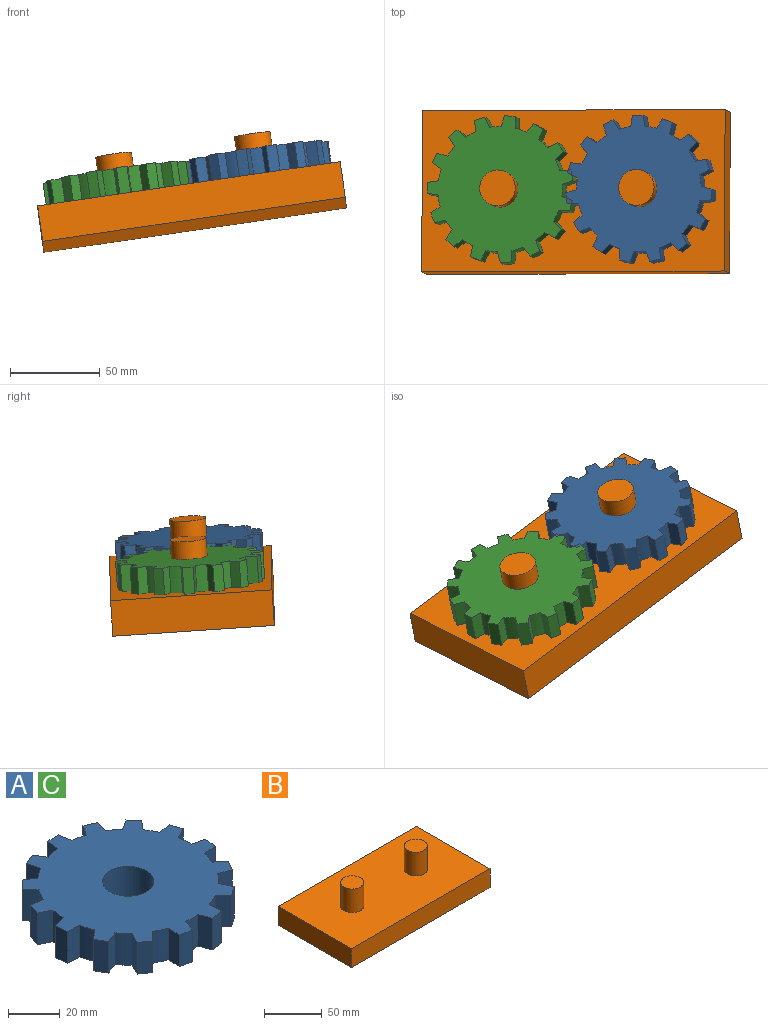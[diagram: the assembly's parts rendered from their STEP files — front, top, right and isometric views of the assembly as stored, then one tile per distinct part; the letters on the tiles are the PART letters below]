
ASSEMBLY  parts=3 mates=2
PART A: 63 faces, bbox 82.2x81.7x15 mm
  f0: plane 15x5.48mm, normal (-0.41,0.91,0), area 90mm2, adj f1,f2,f3,f4
  f1: plane 15x6.1mm, normal (-0.97,-0.26,0), area 94.6mm2, adj f0,f3,f4,f5
  f2: plane 15x5.29mm, normal (0.84,0.55,0), area 94.6mm2, adj f0,f3,f4,f61
  f3: plane 82.18x81.73mm, normal (0,0,1), area 4169.7mm2, adj f0,f1,f2,f5,f6,f7,f8,f9
  f4: plane 82.18x81.73mm, normal (0,0,-1), area 4169.7mm2, adj f0,f1,f2,f5,f6,f7,f8,f9
  f5: cylinder r=35mm len=15mm, axis (0,0,-1), area 99.7mm2, adj f1,f3,f4,f8
  f6: plane 15x4.46mm, normal (-0.74,0.67,0), area 90mm2, adj f3,f4,f7,f8
  f7: plane 15x4.91mm, normal (-0.78,-0.63,0), area 94.6mm2, adj f3,f4,f6,f9
  f8: plane 15x5.29mm, normal (0.54,0.84,0), area 94.6mm2, adj f3,f4,f5,f6
  f9: cylinder r=35mm len=15mm, axis (0,0,-1), area 99.7mm2, adj f3,f4,f7,f12
  f10: plane 15x5.71mm, normal (-0.95,0.31,0), area 90mm2, adj f3,f4,f11,f12
  f11: plane 15x5.62mm, normal (-0.46,-0.89,0), area 94.6mm2, adj f3,f4,f10,f13
  f12: plane 15x6.23mm, normal (0.16,0.99,0), area 94.6mm2, adj f3,f4,f9,f10
  f13: cylinder r=35mm len=15mm, axis (0,0,-1), area 99.7mm2, adj f3,f4,f11,f16
  f14: plane 15x5.97mm, normal (-0.99,-0.1,0), area 90mm2, adj f3,f4,f15,f16
  f15: plane 15x6.3mm, normal (-0.05,-1,0), area 94.6mm2, adj f3,f4,f14,f17
  f16: plane 15x6.09mm, normal (-0.26,0.97,0), area 94.6mm2, adj f3,f4,f13,f14
  f17: cylinder r=35mm len=15mm, axis (0,0,-1), area 99.7mm2, adj f3,f4,f15,f20
  f18: plane 15x5.2mm, normal (-0.87,-0.5,0), area 90mm2, adj f3,f4,f19,f20
  f19: plane 15x5.89mm, normal (0.36,-0.93,0), area 94.6mm2, adj f3,f4,f18,f21
  f20: plane 15x4.9mm, normal (-0.63,0.78,0), area 94.6mm2, adj f3,f4,f17,f18
  f21: cylinder r=35mm len=15mm, axis (0,0,-1), area 99.7mm2, adj f3,f4,f19,f24
  f22: plane 15x4.85mm, normal (-0.59,-0.81,0), area 90mm2, adj f3,f4,f23,f24
  f23: plane 15x4.47mm, normal (0.71,-0.71,0), area 94.6mm2, adj f3,f4,f22,f25
  f24: plane 15x5.62mm, normal (-0.89,0.45,0), area 94.6mm2, adj f3,f4,f21,f22
  f25: cylinder r=35mm len=15mm, axis (0,0,-1), area 99.7mm2, adj f3,f4,f23,f28
  f26: plane 15x5.87mm, normal (-0.21,-0.98,0), area 90mm2, adj f3,f4,f27,f28
  f27: plane 15x5.89mm, normal (0.93,-0.36,0), area 94.6mm2, adj f3,f4,f26,f29
  f28: plane 15x6.3mm, normal (-1,0.05,0), area 94.6mm2, adj f3,f4,f25,f26
  f29: cylinder r=35mm len=15mm, axis (0,0,-1), area 99.7mm2, adj f3,f4,f27,f32
  f30: plane 15x5.87mm, normal (0.21,-0.98,0), area 90mm2, adj f3,f4,f31,f32
  f31: plane 15x6.3mm, normal (1,0.05,0), area 94.6mm2, adj f3,f4,f30,f33
  f32: plane 15x5.89mm, normal (-0.93,-0.36,0), area 94.6mm2, adj f3,f4,f29,f30
  f33: cylinder r=35mm len=15mm, axis (0,0,-1), area 99.7mm2, adj f3,f4,f31,f36
  f34: plane 15x4.85mm, normal (0.59,-0.81,0), area 90mm2, adj f3,f4,f35,f36
  f35: plane 15x5.63mm, normal (0.89,0.45,0), area 94.6mm2, adj f3,f4,f34,f37
  f36: plane 15x4.46mm, normal (-0.71,-0.71,0), area 94.6mm2, adj f3,f4,f33,f34
  f37: cylinder r=35mm len=15mm, axis (0,0,-1), area 99.7mm2, adj f3,f4,f35,f40
  f38: plane 15x5.2mm, normal (0.87,-0.5,0), area 90mm2, adj f3,f4,f39,f40
  f39: plane 15x4.89mm, normal (0.63,0.78,0), area 94.6mm2, adj f3,f4,f38,f41
  f40: plane 15x5.89mm, normal (-0.36,-0.93,0), area 94.6mm2, adj f3,f4,f37,f38
  f41: cylinder r=35mm len=15mm, axis (0,0,-1), area 99.7mm2, adj f3,f4,f39,f44
  f42: plane 15x5.97mm, normal (0.99,-0.1,0), area 90mm2, adj f3,f4,f43,f44
  f43: plane 15x6.09mm, normal (0.26,0.97,0), area 94.6mm2, adj f3,f4,f42,f45
  f44: plane 15x6.3mm, normal (0.05,-1,0), area 94.6mm2, adj f3,f4,f41,f42
  f45: cylinder r=35mm len=15mm, axis (0,0,-1), area 99.7mm2, adj f3,f4,f43,f48
  f46: plane 15x5.71mm, normal (0.95,0.31,0), area 90mm2, adj f3,f4,f47,f48
  f47: plane 15x6.23mm, normal (-0.15,0.99,0), area 94.6mm2, adj f3,f4,f46,f49
  f48: plane 15x5.62mm, normal (0.45,-0.89,0), area 94.6mm2, adj f3,f4,f45,f46
  f49: cylinder r=35mm len=15mm, axis (0,0,-1), area 99.7mm2, adj f3,f4,f47,f52
  f50: plane 15x4.46mm, normal (0.74,0.67,0), area 90mm2, adj f3,f4,f51,f52
  f51: plane 15x5.3mm, normal (-0.54,0.84,0), area 94.6mm2, adj f3,f4,f50,f53
  f52: plane 15x4.91mm, normal (0.78,-0.63,0), area 94.6mm2, adj f3,f4,f49,f50
  f53: cylinder r=35mm len=15mm, axis (0,0,-1), area 99.7mm2, adj f3,f4,f51,f56
  f54: plane 15x5.48mm, normal (0.41,0.91,0), area 90mm2, adj f3,f4,f55,f56
  f55: plane 15x5.28mm, normal (-0.84,0.55,0), area 94.6mm2, adj f3,f4,f54,f57
  f56: plane 15x6.09mm, normal (0.97,-0.26,0), area 94.6mm2, adj f3,f4,f53,f54
  f57: cylinder r=35mm len=15mm, axis (0,0,-1), area 99.7mm2, adj f3,f4,f55,f60
  f58: plane 15x6mm, normal (0,1,0), area 90mm2, adj f3,f4,f59,f60
  f59: plane 15x6.23mm, normal (-0.99,0.16,0), area 94.6mm2, adj f3,f4,f58,f61
  f60: plane 15x6.23mm, normal (0.99,0.16,0), area 94.6mm2, adj f3,f4,f57,f58
  f61: cylinder r=35mm len=15mm, axis (0,0,-1), area 99.7mm2, adj f2,f3,f4,f59
  f62: cylinder r=10mm len=20mm, axis (0,0,1), area 942.5mm2, adj f3,f4
PART B: 10 faces, bbox 170x90x45 mm
  f0: plane 170x20mm, normal (0,1,0), area 3400mm2, adj f1,f3,f4,f5
  f1: plane 90x20mm, normal (-1,0,0), area 1800mm2, adj f0,f2,f4,f5
  f2: plane 170x20mm, normal (0,-1,0), area 3400mm2, adj f1,f3,f4,f5
  f3: plane 90x20mm, normal (1,0,0), area 1800mm2, adj f0,f2,f4,f5
  f4: plane 170x90mm, normal (0,0,1), area 14671.7mm2, adj f0,f1,f2,f3,f6,f8
  f5: plane 170x90mm, normal (0,0,-1), area 15300mm2, adj f0,f1,f2,f3
  f6: cylinder r=10mm len=25mm, axis (0,0,-1), area 1570.8mm2, adj f4,f7
  f7: plane 20x20mm, normal (0,0,1), area 314.2mm2, adj f6
  f8: cylinder r=10mm len=25mm, axis (0,0,-1), area 1570.8mm2, adj f4,f9
  f9: plane 20x20mm, normal (0,0,1), area 314.2mm2, adj f8
PART C: same geometry as A
PLACE A rot(axis=(-0.09,-0.37,-0.93),24.6deg) t=(34.53,35.65,-31.05)mm
PLACE B rot(axis=(-0.42,-0.91,-0.01),9.2deg) t=(-1.16,34.19,-56.44)mm
PLACE C rot(axis=(-0.09,-0.01,1),112.8deg) t=(-42.64,35.42,-42.35)mm
MATE revolute C.f62 <-> B.f6  axis (0.14,-0.07,-0.99) through (-42.64,35.42,-42.35)mm
MATE revolute A.f62 <-> B.f8  axis (0.14,-0.07,-0.99) through (34.53,35.65,-31.05)mm
